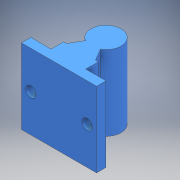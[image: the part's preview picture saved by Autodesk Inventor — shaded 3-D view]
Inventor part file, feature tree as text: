
AUTODESK INVENTOR PART (.ipt)
format: ipt  version: 2018 (Build 220112000, 112)  size: 145,920 bytes
history: native  units: mm
features: sketch x2, other x1, extrude x1, hole x1
ambient origin geometry x8: Origin, YZ Plane, XZ Plane, XY Plane, X Axis, Y Axis, Z Axis, Center Point
bodies: Body1 (feature_tree)
feature tree (5):
  other  "Sólido1"
  extrude  "Extrusão1"  Depth=25.0mm
  hole  "Furo1"  [1 undecoded]
  sketch  "Esboço1"  dims[d6=16.0mm d7=25.0mm]
  sketch  "Esboço3"  dims[d8=18.5mm d9=11.7mm d10=8.0mm d11=30.0deg d12=30.0deg d13=5.0mm d14=40.0mm d15=40.0mm d16=0.0mm d18=15.0mm d19=15.0mm d20=5.5mm d21=5.5mm d22=20.0mm d28=5.5mm d29=6.0mm d30=4.0mm d31=2.0mm d32=90.0deg d33=8.0mm d34=20.594885mm]
note: 1 required parameter value undecoded (feature->parameter linkage not recoverable at this tier; creation-order binding heuristic only, values carry confidence <= 0.55)
